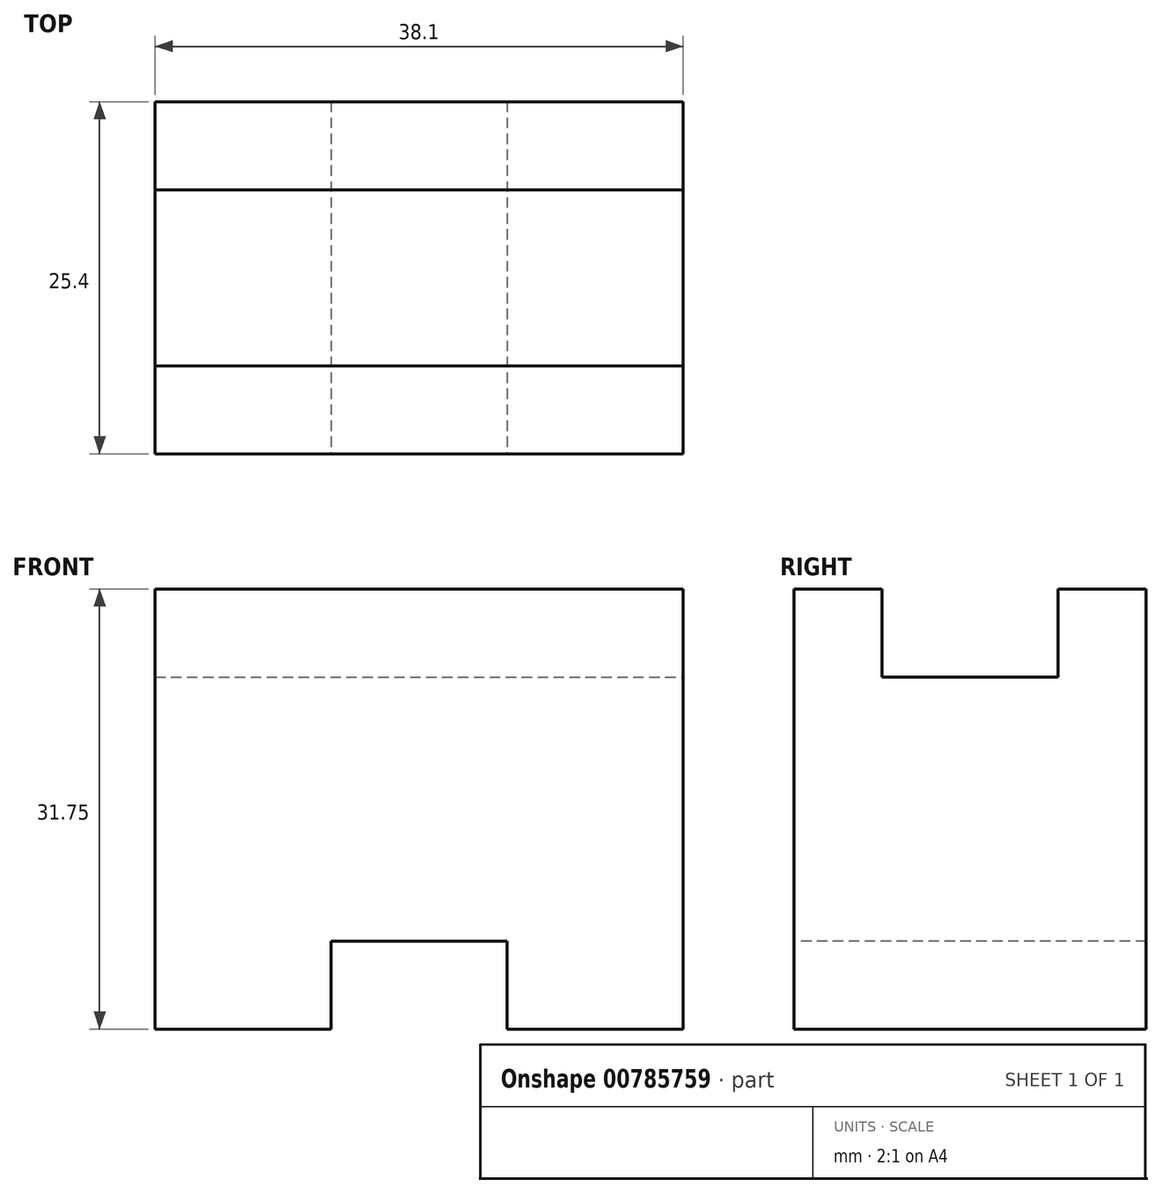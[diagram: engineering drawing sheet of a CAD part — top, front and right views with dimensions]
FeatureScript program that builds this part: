
annotation { "Feature Type Name" : "Feature", "Feature Type Description" : "" }
export const myFeature = defineFeature(function(context is Context, id is Id, definition is map)
    precondition{}
    {
        {
            var Q0;
            Q0=qCreatedBy(makeId("Front.planeOp"),FACE);
            var sketch = newSketch(context, id + "F0", { "sketchPlane" : qUnion([Q0])});
            skLineSegment(sketch, "E0", {"start": v(0, 0) * mm, "end": v(19.05, 0) * mm});
            skLineSegment(sketch, "E1", {"start": v(19.05, 31.75) * mm, "end": v(19.05, 0) * mm});
            skLineSegment(sketch, "E2", {"start": v(19.05, 31.75) * mm, "end": v(-19.05, 31.75) * mm});
            skLineSegment(sketch, "E3", {"start": v(-19.05, 31.75) * mm, "end": v(-19.05, 0) * mm});
            skLineSegment(sketch, "E4", {"start": v(0, 0) * mm, "end": v(-19.05, 0) * mm});
            skSolve(sketch);
        }
        {
            var Q0;
            Q0=makeQuery(id+"F0.imprint","IMPRINT",FACE,{"disambiguationData":[TD([[makeQuery(id+"F0.imprint","IMPRINT",EDGE,{"derivedFrom":sQuery(id+"F0.wireOp",EDGE,"E0")}),1.0]])]});
            extrude(context, id + "F1", {"entities" : qUnion([Q0]), "depth" : 25.4 * mm, "offsetDistance" : 25.4 * mm});
        }
        {
            var Q0;
            Q0=makeQuery(id+"F1.opExtrude","SWEPT_FACE",FACE,{"disambiguationData":[OSD([sQuery(id+"F0.wireOp",EDGE,"E1")])]});
            var sketch = newSketch(context, id + "F2", { "sketchPlane" : qUnion([Q0])});
            skLineSegment(sketch, "E5", {"start": v(0, 31.75) * mm, "end": v(-6.35, 31.75) * mm});
            skLineSegment(sketch, "E6", {"start": v(-6.35, 31.75) * mm, "end": v(-6.35, 25.4) * mm});
            skLineSegment(sketch, "E7", {"start": v(-6.35, 25.4) * mm, "end": v(-19.05, 25.4) * mm});
            skLineSegment(sketch, "E8", {"start": v(-19.05, 25.4) * mm, "end": v(-19.05, 31.75) * mm});
            skLineSegment(sketch, "E9", {"start": v(-19.05, 31.75) * mm, "end": v(-6.35, 31.75) * mm});
            skSolve(sketch);
        }
        {
            var Q0;
            Q0=makeQuery(id+"F2.imprint","IMPRINT",FACE,{"disambiguationData":[TD([[makeQuery(id+"F2.imprint","IMPRINT",EDGE,{"derivedFrom":sQuery(id+"F2.wireOp",EDGE,"E6")}),-1.0]])]});
            extrude(context, id + "F3", {"entities" : qUnion([Q0]), "operationType" : NewBodyOperationType.REMOVE, "oppositeDirection" : true, "depth" : 38.1 * mm, "offsetDistance" : 25.4 * mm});
        }
        {
            var Q0;
            Q0=makeQuery(id+"F1.opExtrude","CAP_FACE",FACE,{"disambiguationData":[OSD([sQuery(id+"F0.wireOp",EDGE,"E0"),sQuery(id+"F0.wireOp",EDGE,"E1"),sQuery(id+"F0.wireOp",EDGE,"E2"),sQuery(id+"F0.wireOp",EDGE,"E3"),sQuery(id+"F0.wireOp",EDGE,"E4")])],"isStart":false});
            var sketch = newSketch(context, id + "F4", { "sketchPlane" : qUnion([Q0])});
            skLineSegment(sketch, "E10", {"start": v(-19.05, 0) * mm, "end": v(-6.35, 0) * mm});
            skLineSegment(sketch, "E11", {"start": v(-6.35, 0) * mm, "end": v(-6.35, 6.35) * mm});
            skLineSegment(sketch, "E12", {"start": v(-6.35, 6.35) * mm, "end": v(6.35, 6.35) * mm});
            skLineSegment(sketch, "E13", {"start": v(6.35, 6.35) * mm, "end": v(6.35, 0) * mm});
            skLineSegment(sketch, "E14", {"start": v(6.35, 0) * mm, "end": v(-6.35, 0) * mm});
            skSolve(sketch);
        }
        {
            var Q0;
            Q0=makeQuery(id+"F4.imprint","IMPRINT",FACE,{"disambiguationData":[TD([[makeQuery(id+"F4.imprint","IMPRINT",EDGE,{"derivedFrom":sQuery(id+"F4.wireOp",EDGE,"E11")}),-1.0]])]});
            extrude(context, id + "F5", {"entities" : qUnion([Q0]), "operationType" : NewBodyOperationType.REMOVE, "oppositeDirection" : true, "depth" : 25.4 * mm, "offsetDistance" : 25.4 * mm});
        }
    });
